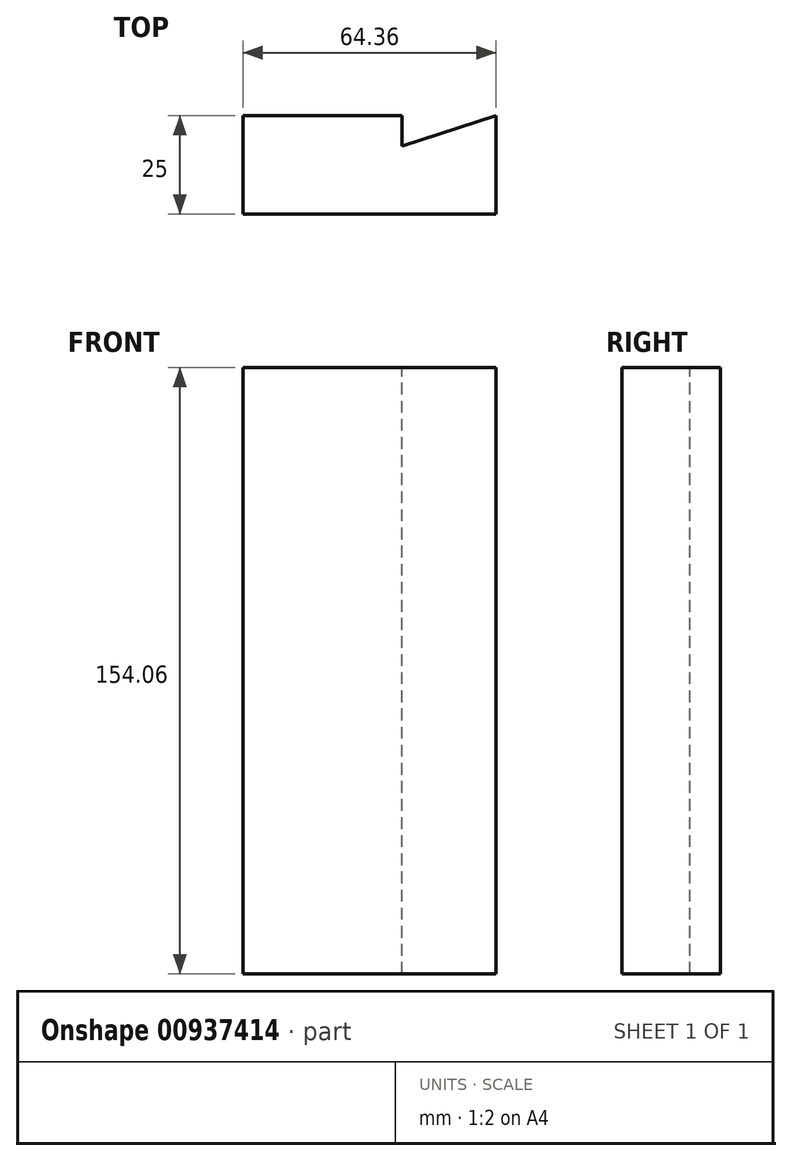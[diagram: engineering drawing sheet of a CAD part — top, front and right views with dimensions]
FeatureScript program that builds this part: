
annotation { "Feature Type Name" : "Feature", "Feature Type Description" : "" }
export const myFeature = defineFeature(function(context is Context, id is Id, definition is map)
    precondition{}
    {
        {
            var Q0;
            Q0=qCreatedBy(makeId("Front.planeOp"),FACE);
            var sketch = newSketch(context, id + "F0", { "sketchPlane" : qUnion([Q0])});
            skLineSegment(sketch, "E0.bottom", {"start": v(32.18, 77.03) * mm, "end": v(-32.18, 77.03) * mm});
            skLineSegment(sketch, "E0.top", {"start": v(32.18, -77.03) * mm, "end": v(-32.18, -77.03) * mm});
            skLineSegment(sketch, "E0.left", {"start": v(32.18, 77.03) * mm, "end": v(32.18, -77.03) * mm});
            skLineSegment(sketch, "E0.right", {"start": v(-32.18, 77.03) * mm, "end": v(-32.18, -77.03) * mm});
            skPoint(sketch, "E0.middle", {"position": v(0, 0) * mm});
            skSolve(sketch);
        }
        {
            var Q0;
            Q0=makeQuery(id+"F0.imprint","IMPRINT",FACE,{"disambiguationData":[TD([[makeQuery(id+"F0.imprint","IMPRINT",EDGE,{"derivedFrom":sQuery(id+"F0.wireOp",EDGE,"E0.bottom")}),1.0]])]});
            extrude(context, id + "F1", {"entities" : qUnion([Q0]), "oppositeDirection" : true, "depth" : 25 * mm, "offsetDistance" : 25 * mm});
        }
        {
            var Q0;
            Q0=makeQuery(id+"F1.opExtrude","SWEPT_FACE",FACE,{"disambiguationData":[OSD([sQuery(id+"F0.wireOp",EDGE,"E0.bottom")])]});
            var sketch = newSketch(context, id + "F2", { "sketchPlane" : qUnion([Q0])});
            skLineSegment(sketch, "E1", {"start": v(32.18, 25) * mm, "end": v(8.24, 17.22) * mm});
            skLineSegment(sketch, "E2", {"start": v(8.24, 17.22) * mm, "end": v(8.24, 25) * mm});
            skLineSegment(sketch, "E3", {"start": v(8.24, 25) * mm, "end": v(32.18, 25) * mm});
            skSolve(sketch);
        }
        {
            var Q0;
            Q0=makeQuery(id+"F2.imprint","IMPRINT",FACE,{"disambiguationData":[TD([[makeQuery(id+"F2.imprint","IMPRINT",EDGE,{"derivedFrom":sQuery(id+"F2.wireOp",EDGE,"E1")}),-1.0]])]});
            var Q1;
            Q1 = qSketchRegion(id + "F2", true);
            extrude(context, id + "F3", {"entities" : qUnion([Q0, Q1]), "operationType" : NewBodyOperationType.REMOVE, "endBound" : BoundingType.UP_TO_NEXT, "oppositeDirection" : true, "depth" : 25 * mm, "offsetDistance" : 25 * mm});
        }
    });
